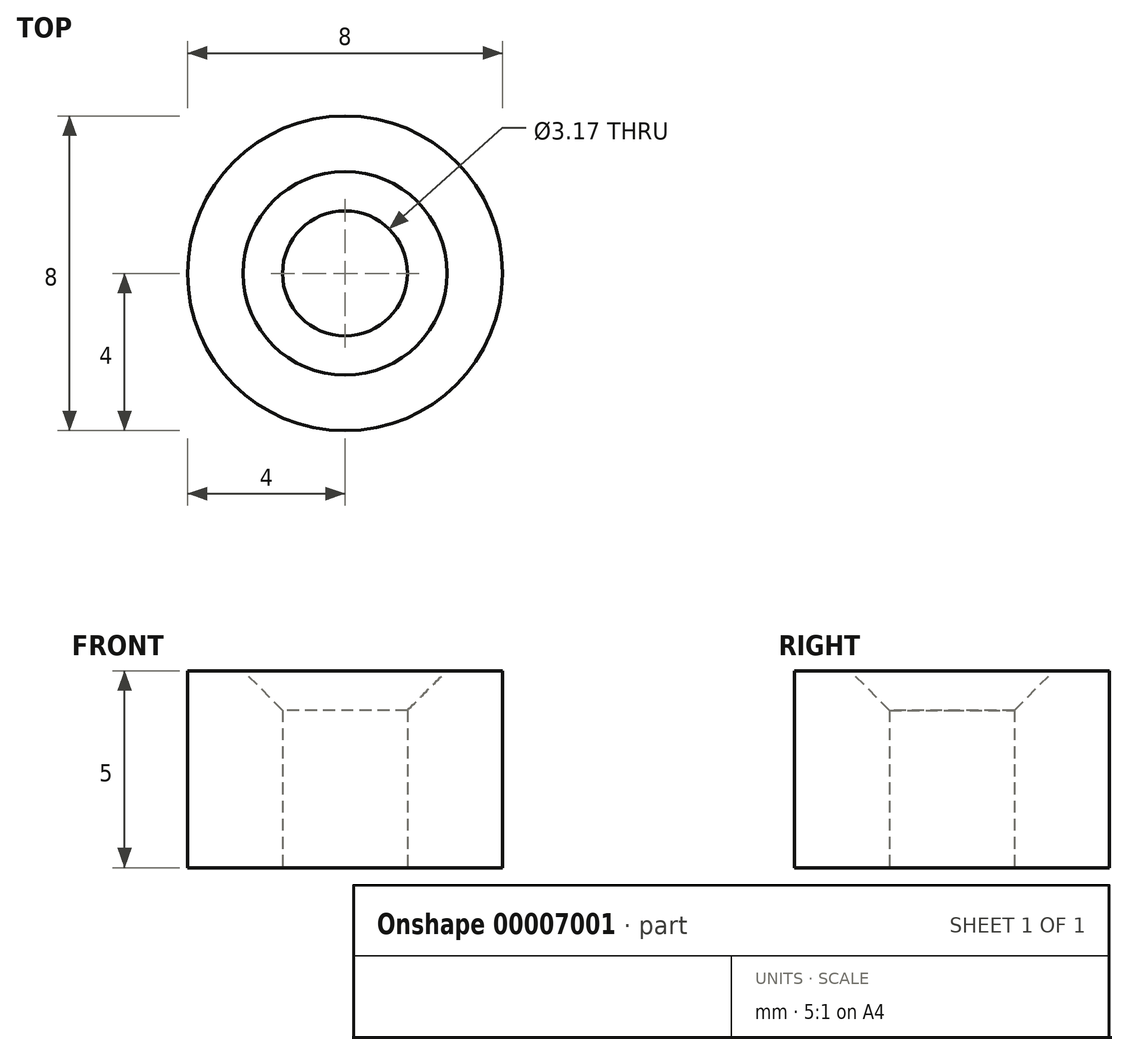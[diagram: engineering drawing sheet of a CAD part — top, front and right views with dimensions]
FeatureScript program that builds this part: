
annotation { "Feature Type Name" : "Feature", "Feature Type Description" : "" }
export const myFeature = defineFeature(function(context is Context, id is Id, definition is map)
    precondition{}
    {
        {
            var Q0;
            Q0=qCreatedBy(makeId("Top.planeOp"),FACE);
            var sketch = newSketch(context, id + "F0", { "sketchPlane" : qUnion([Q0])});
            skCircle(sketch, "E0", {"center": v(0, 0) * mm, "radius": 1.59 * mm});
            skCircle(sketch, "E1", {"center": v(0, 0) * mm, "radius": 4 * mm});
            skSolve(sketch);
        }
        {
            var Q0;
            Q0 = qSketchRegion(id + "F0", true);
            extrude(context, id + "F1", {"entities" : qUnion([Q0]), "depth" : 5 * mm});
        }
        {
            var Q0;
            Q0=makeQuery(id+"F1.opExtrude","CAP_EDGE",EDGE,{"disambiguationData":[OSD([sQuery(id+"F0.wireOp",EDGE,"E0")])],"isStart":false});
            chamfer(context, id + "F2", {"entities" : qUnion([Q0]), "width" : 1 * mm});
        }
    });
